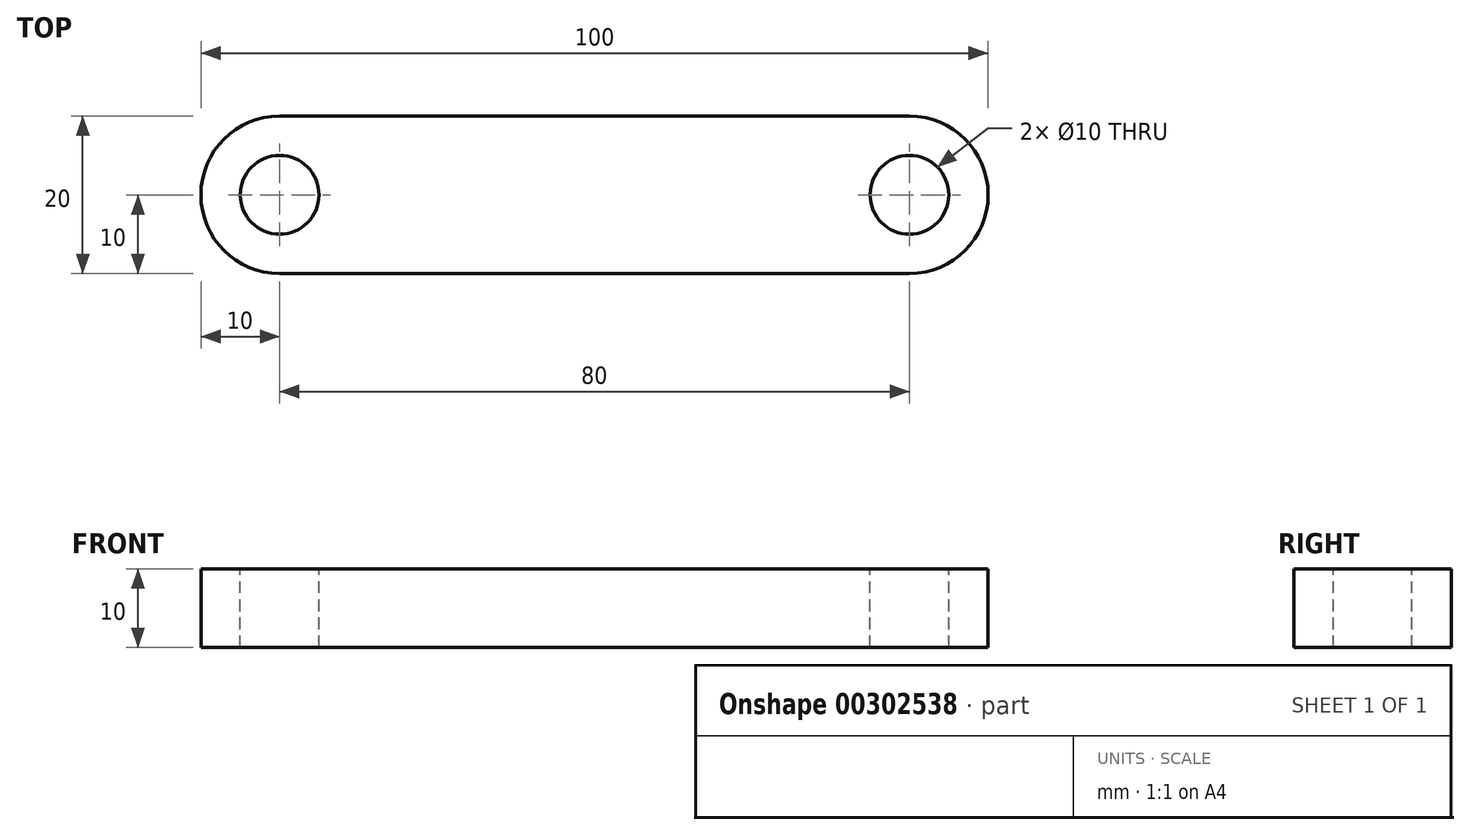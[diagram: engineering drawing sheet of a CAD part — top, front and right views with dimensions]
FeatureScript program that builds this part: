
annotation { "Feature Type Name" : "Feature", "Feature Type Description" : "" }
export const myFeature = defineFeature(function(context is Context, id is Id, definition is map)
    precondition{}
    {
        {
            var Q0;
            Q0=qCreatedBy(makeId("Top.planeOp"),FACE);
            var sketch = newSketch(context, id + "F0", { "sketchPlane" : qUnion([Q0])});
            skLineSegment(sketch, "E0.bottom", {"start": v(0, 0) * mm, "end": v(80, 0) * mm, "construction": true});
            skLineSegment(sketch, "E0.top", {"start": v(0, 20) * mm, "end": v(80, 20) * mm, "construction": true});
            skLineSegment(sketch, "E0.left", {"start": v(0, 0) * mm, "end": v(0, 20) * mm, "construction": true});
            skLineSegment(sketch, "E0.right", {"start": v(80, 0) * mm, "end": v(80, 20) * mm, "construction": true});
            skLineSegment(sketch, "E1", {"start": v(0, 20) * mm, "end": v(80, 20) * mm});
            skLineSegment(sketch, "E2", {"start": v(80, 0) * mm, "end": v(0, 0) * mm});
            skArc(sketch, "E3", {"start": v(0, 20) * mm, "mid": v(-10, 10) * mm, "end": v(0, 0) * mm});
            skArc(sketch, "E4", {"start": v(80, 0) * mm, "mid": v(90, 10) * mm, "end": v(80, 20) * mm});
            skCircle(sketch, "E5", {"center": v(0, 10) * mm, "radius": 5 * mm});
            skCircle(sketch, "E6", {"center": v(80, 10) * mm, "radius": 5 * mm});
            skSolve(sketch);
        }
        {
            var Q0;
            Q0=makeQuery(id+"F0.imprint","IMPRINT",FACE,{"disambiguationData":[TD([[makeQuery(id+"F0.imprint","IMPRINT",EDGE,{"derivedFrom":sQuery(id+"F0.wireOp",EDGE,"E1")}),-1.0]])]});
            extrude(context, id + "F1", {"entities" : qUnion([Q0]), "oppositeDirection" : true, "depth" : 10 * mm});
        }
    });
